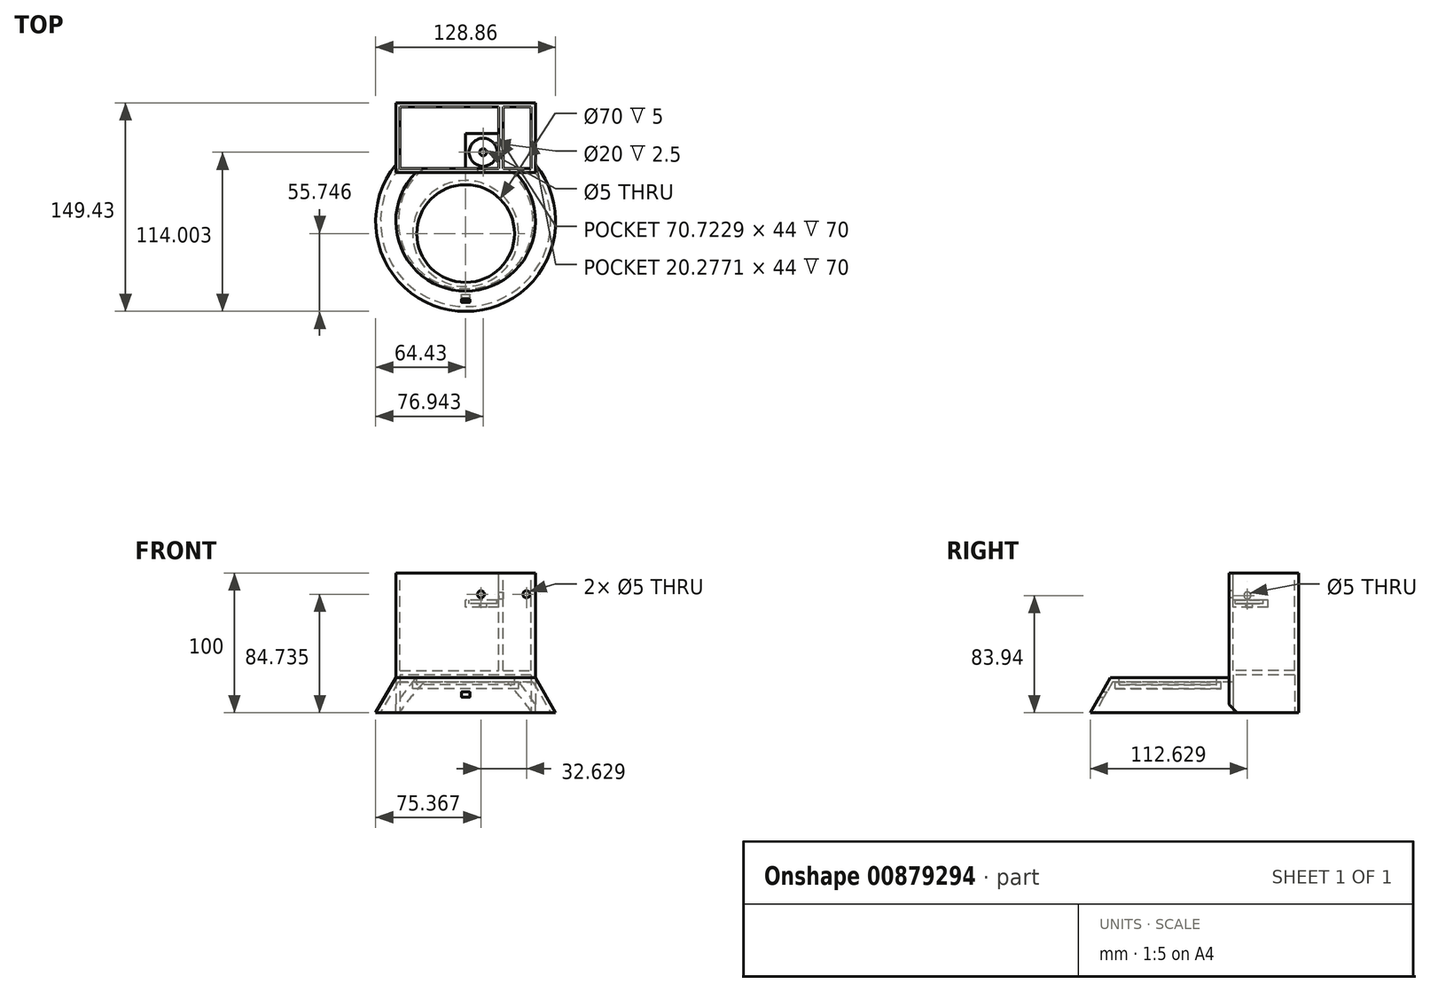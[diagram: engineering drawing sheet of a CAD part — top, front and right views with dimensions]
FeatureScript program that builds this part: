
annotation { "Feature Type Name" : "Feature", "Feature Type Description" : "" }
export const myFeature = defineFeature(function(context is Context, id is Id, definition is map)
    precondition{}
    {
        {
            var Q0;
            Q0=qCreatedBy(makeId("Top.planeOp"),FACE);
            var sketch = newSketch(context, id + "F0", { "sketchPlane" : qUnion([Q0])});
            skCircle(sketch, "E0", {"center": v(0, 0) * mm, "radius": 50 * mm});
            skSolve(sketch);
        }
        {
            var Q0;
            Q0 = qSketchRegion(id + "F0", true);
            extrude(context, id + "F1", {"entities" : qUnion([Q0]), "oppositeDirection" : true, "depth" : 25 * mm, "offsetDistance" : 25 * mm, "hasDraft" : true, "draftAngle" : 30 * degree});
        }
        {
            var Q0;
            Q0=makeQuery(id+"F1.opExtrude","CAP_FACE",FACE,{"disambiguationData":[OSD([sQuery(id+"F0.wireOp",EDGE,"E0")])],"isStart":false});
            var sketch = newSketch(context, id + "F2", { "sketchPlane" : qUnion([Q0])});
            skLineSegment(sketch, "E1.bottom", {"start": v(-50, -35) * mm, "end": v(50, -35) * mm});
            skLineSegment(sketch, "E1.top", {"start": v(-50, -85) * mm, "end": v(50, -85) * mm});
            skLineSegment(sketch, "E1.left", {"start": v(-50, -35) * mm, "end": v(-50, -85) * mm});
            skLineSegment(sketch, "E1.right", {"start": v(50, -35) * mm, "end": v(50, -85) * mm});
            skSolve(sketch);
        }
        {
            var Q0;
            {var subQ0=sQuery(id+"F2.wireOp",EDGE,"E1.bottom");Q0=makeQuery(id+"F2.imprint","IMPRINT",FACE,{"disambiguationData":[TD([[makeQuery(id+"F2.imprint","IMPRINT",EDGE,{"derivedFrom":subQ0}),-1.0]])]});}
            var Q1;
            {var subQ0=sQuery(id+"F2.wireOp",EDGE,"E1.top");Q1=makeQuery(id+"F2.imprint","IMPRINT",FACE,{"disambiguationData":[TD([[makeQuery(id+"F2.imprint","IMPRINT",EDGE,{"derivedFrom":subQ0}),1.0]])]});}
            extrude(context, id + "F3", {"entities" : qUnion([Q0, Q1]), "operationType" : NewBodyOperationType.ADD, "oppositeDirection" : true, "depth" : 100 * mm, "offsetDistance" : 25 * mm});
        }
        {
            var Q0;
            Q0=makeQuery(id+"F1.opExtrude","CAP_FACE",FACE,{"disambiguationData":[OSD([sQuery(id+"F0.wireOp",EDGE,"E0")])],"isStart":true});
            var sketch = newSketch(context, id + "F4", { "sketchPlane" : qUnion([Q0])});
            skCircle(sketch, "E2", {"center": v(0, -8.68) * mm, "radius": 35 * mm});
            skSolve(sketch);
        }
        {
            var Q0;
            Q0=makeQuery(id+"F4.imprint","IMPRINT",FACE,{"disambiguationData":[TD([[makeQuery(id+"F4.imprint","IMPRINT",EDGE,{"derivedFrom":sQuery(id+"F4.wireOp",EDGE,"E2")}),1.0]])]});
            extrude(context, id + "F5", {"entities" : qUnion([Q0]), "operationType" : NewBodyOperationType.REMOVE, "oppositeDirection" : true, "depth" : 5 * mm, "offsetDistance" : 25 * mm});
        }
        {
            var Q0;
            Q0=makeQuery(id+"F3.opExtrude","CAP_FACE",FACE,{"disambiguationData":[OSD([sQuery(id+"F2.wireOp",EDGE,"E1.bottom"),sQuery(id+"F2.wireOp",EDGE,"E1.top"),sQuery(id+"F2.wireOp",EDGE,"E1.left"),sQuery(id+"F2.wireOp",EDGE,"E1.right")])],"isStart":false});
            var sketch = newSketch(context, id + "F6", { "sketchPlane" : qUnion([Q0])});
            skLineSegment(sketch, "E3.bottom", {"start": v(-47, 82) * mm, "end": v(23.72, 82) * mm});
            skLineSegment(sketch, "E3.top", {"start": v(-47, 38) * mm, "end": v(23.72, 38) * mm});
            skLineSegment(sketch, "E3.left", {"start": v(-47, 82) * mm, "end": v(-47, 38) * mm});
            skLineSegment(sketch, "E3.right", {"start": v(23.72, 82) * mm, "end": v(23.72, 38) * mm});
            skSolve(sketch);
        }
        {
            var Q0;
            Q0=makeQuery(id+"F6.imprint","IMPRINT",FACE,{"disambiguationData":[TD([[makeQuery(id+"F6.imprint","IMPRINT",EDGE,{"derivedFrom":sQuery(id+"F6.wireOp",EDGE,"E3.bottom")}),-1.0]])]});
            extrude(context, id + "F7", {"entities" : qUnion([Q0]), "operationType" : NewBodyOperationType.REMOVE, "oppositeDirection" : true, "depth" : 70 * mm, "offsetDistance" : 25 * mm});
        }
        {
            var Q0;
            Q0=makeQuery(id+"F3.opExtrude","CAP_FACE",FACE,{"disambiguationData":[OSD([sQuery(id+"F2.wireOp",EDGE,"E1.bottom"),sQuery(id+"F2.wireOp",EDGE,"E1.top"),sQuery(id+"F2.wireOp",EDGE,"E1.left"),sQuery(id+"F2.wireOp",EDGE,"E1.right")])],"isStart":false});
            var sketch = newSketch(context, id + "F8", { "sketchPlane" : qUnion([Q0])});
            skLineSegment(sketch, "E4.bottom", {"start": v(26.72, 82) * mm, "end": v(47, 82) * mm});
            skLineSegment(sketch, "E4.top", {"start": v(26.72, 38) * mm, "end": v(47, 38) * mm});
            skLineSegment(sketch, "E4.left", {"start": v(26.72, 82) * mm, "end": v(26.72, 38) * mm});
            skLineSegment(sketch, "E4.right", {"start": v(47, 82) * mm, "end": v(47, 38) * mm});
            skSolve(sketch);
        }
        {
            var Q0;
            Q0=makeQuery(id+"F8.imprint","IMPRINT",FACE,{"disambiguationData":[TD([[makeQuery(id+"F8.imprint","IMPRINT",EDGE,{"derivedFrom":sQuery(id+"F8.wireOp",EDGE,"E4.bottom")}),-1.0]])]});
            extrude(context, id + "F9", {"entities" : qUnion([Q0]), "operationType" : NewBodyOperationType.REMOVE, "oppositeDirection" : true, "depth" : 70 * mm, "offsetDistance" : 25 * mm});
        }
        {
            var Q0;
            Q0=makeQuery(id+"F3.boolean.opBoolean","MERGE",FACE,{"derivedFrom":[makeQuery(id+"F1.opExtrude","CAP_FACE",FACE,{"disambiguationData":[OSD([sQuery(id+"F0.wireOp",EDGE,"E0")])],"isStart":false}),makeQuery(id+"F3.opExtrude","CAP_FACE",FACE,{"disambiguationData":[OSD([sQuery(id+"F2.wireOp",EDGE,"E1.bottom"),sQuery(id+"F2.wireOp",EDGE,"E1.top"),sQuery(id+"F2.wireOp",EDGE,"E1.left"),sQuery(id+"F2.wireOp",EDGE,"E1.right")])],"isStart":true})]});
            shell(context, id + "F10", {"entities" : qUnion([Q0]), "thickness" : 3 * mm});
        }
        {
            var Q0;
            Q0=makeQuery(id+"F9.boolean.opBoolean","COPY",FACE,{"derivedFrom":makeQuery(id+"F9.opExtrude","SWEPT_FACE",FACE,{"disambiguationData":[OSD([sQuery(id+"F8.wireOp",EDGE,"E4.left")])]})});
            var sketch = newSketch(context, id + "F11", { "sketchPlane" : qUnion([Q0])});
            skCircle(sketch, "E5", {"center": v(48.2, 58.94) * mm, "radius": 2.5 * mm});
            skSolve(sketch);
        }
        {
            var Q0;
            Q0=makeQuery(id+"F3.opExtrude","SWEPT_FACE",FACE,{"disambiguationData":[OSD([sQuery(id+"F2.wireOp",EDGE,"E1.bottom")])]});
            var sketch = newSketch(context, id + "F12", { "sketchPlane" : qUnion([Q0])});
            skCircle(sketch, "E6", {"center": v(10.94, 59.73) * mm, "radius": 2.5 * mm});
            skCircle(sketch, "E7", {"center": v(43.57, 59.73) * mm, "radius": 2.5 * mm});
            skSolve(sketch);
        }
        {
            var Q0;
            Q0=makeQuery(id+"F12.imprint","IMPRINT",FACE,{"disambiguationData":[TD([[makeQuery(id+"F12.imprint","IMPRINT",EDGE,{"derivedFrom":sQuery(id+"F12.wireOp",EDGE,"E6")}),1.0]])]});
            var Q1;
            Q1=makeQuery(id+"F12.imprint","IMPRINT",FACE,{"disambiguationData":[TD([[makeQuery(id+"F12.imprint","IMPRINT",EDGE,{"derivedFrom":sQuery(id+"F12.wireOp",EDGE,"E7")}),1.0]])]});
            extrude(context, id + "F13", {"entities" : qUnion([Q0, Q1]), "operationType" : NewBodyOperationType.REMOVE, "endBound" : BoundingType.UP_TO_NEXT, "oppositeDirection" : true, "depth" : 25 * mm, "offsetDistance" : 25 * mm});
        }
        {
            var Q0;
            Q0=makeQuery(id+"F11.imprint","IMPRINT",FACE,{"disambiguationData":[TD([[makeQuery(id+"F11.imprint","IMPRINT",EDGE,{"derivedFrom":sQuery(id+"F11.wireOp",EDGE,"E5")}),1.0]])]});
            extrude(context, id + "F14", {"entities" : qUnion([Q0]), "operationType" : NewBodyOperationType.REMOVE, "endBound" : BoundingType.UP_TO_NEXT, "oppositeDirection" : true, "depth" : 25 * mm, "offsetDistance" : 25 * mm});
        }
        {
            var Q0;
            Q0=makeQuery(id+"F7.boolean.opBoolean","COPY",FACE,{"derivedFrom":makeQuery(id+"F7.opExtrude","SWEPT_FACE",FACE,{"disambiguationData":[OSD([sQuery(id+"F6.wireOp",EDGE,"E3.top")])]})});
            var sketch = newSketch(context, id + "F15", { "sketchPlane" : qUnion([Q0])});
            skLineSegment(sketch, "E8.0", {"start": v(-23.72, 5) * mm, "end": v(-23.72, 75) * mm});
            skLineSegment(sketch, "E9.bottom", {"start": v(-23.72, 50.5) * mm, "end": v(0, 50.5) * mm});
            skLineSegment(sketch, "E9.top", {"start": v(-23.72, 55.5) * mm, "end": v(0, 55.5) * mm});
            skLineSegment(sketch, "E9.left", {"start": v(-23.72, 50.5) * mm, "end": v(-23.72, 55.5) * mm});
            skLineSegment(sketch, "E9.right", {"start": v(0, 50.5) * mm, "end": v(0, 55.5) * mm});
            skSolve(sketch);
        }
        {
            var Q0;
            Q0=makeQuery(id+"F15.imprint","IMPRINT",FACE,{"disambiguationData":[TD([[makeQuery(id+"F15.imprint","IMPRINT",EDGE,{"derivedFrom":sQuery(id+"F15.wireOp",EDGE,"E9.bottom")}),1.0]])]});
            extrude(context, id + "F16", {"entities" : qUnion([Q0]), "operationType" : NewBodyOperationType.ADD, "depth" : 25 * mm, "offsetDistance" : 25 * mm});
        }
        {
            var Q0;
            Q0=makeQuery(id+"F16.opExtrude","SWEPT_FACE",FACE,{"disambiguationData":[OSD([sQuery(id+"F15.wireOp",EDGE,"E9.top")])]});
            var sketch = newSketch(context, id + "F17", { "sketchPlane" : qUnion([Q0])});
            skCircle(sketch, "E10", {"center": v(12.51, 49.57) * mm, "radius": 10 * mm});
            skSolve(sketch);
        }
        {
            var Q0;
            Q0=makeQuery(id+"F17.imprint","IMPRINT",FACE,{"disambiguationData":[TD([[makeQuery(id+"F17.imprint","IMPRINT",EDGE,{"derivedFrom":sQuery(id+"F17.wireOp",EDGE,"E10")}),1.0]])]});
            extrude(context, id + "F18", {"entities" : qUnion([Q0]), "operationType" : NewBodyOperationType.REMOVE, "oppositeDirection" : true, "depth" : 2.5 * mm, "offsetDistance" : 25 * mm});
        }
        {
            var Q0;
            Q0=makeQuery(id+"F18.boolean.opBoolean","COPY",FACE,{"derivedFrom":makeQuery(id+"F18.opExtrude","CAP_FACE",FACE,{"disambiguationData":[OSD([sQuery(id+"F17.wireOp",EDGE,"E10")])],"isStart":false})});
            var sketch = newSketch(context, id + "F19", { "sketchPlane" : qUnion([Q0])});
            skCircle(sketch, "E11.0.0", {"center": v(12.51, 49.57) * mm, "radius": 10 * mm});
            skCircle(sketch, "E12", {"center": v(12.51, 49.57) * mm, "radius": 2.5 * mm});
            skSolve(sketch);
        }
        {
            var Q0;
            Q0=makeQuery(id+"F19.imprint","IMPRINT",FACE,{"disambiguationData":[TD([[makeQuery(id+"F19.imprint","IMPRINT",EDGE,{"derivedFrom":sQuery(id+"F19.wireOp",EDGE,"E12")}),1.0]])]});
            extrude(context, id + "F20", {"entities" : qUnion([Q0]), "operationType" : NewBodyOperationType.REMOVE, "endBound" : BoundingType.UP_TO_NEXT, "oppositeDirection" : true, "depth" : 25 * mm, "offsetDistance" : 25 * mm});
        }
        {
            var Q0;
            Q0=qCreatedBy(makeId("Front.planeOp"),FACE);
            var sketch = newSketch(context, id + "F21", { "sketchPlane" : qUnion([Q0])});
            skLineSegment(sketch, "E13.bottom", {"start": v(2.5, -10.03) * mm, "end": v(-2.5, -10.03) * mm});
            skLineSegment(sketch, "E13.top", {"start": v(2.5, -14.03) * mm, "end": v(-2.5, -14.03) * mm});
            skLineSegment(sketch, "E13.left", {"start": v(3, -10.53) * mm, "end": v(3, -13.53) * mm});
            skLineSegment(sketch, "E13.right", {"start": v(-3, -10.53) * mm, "end": v(-3, -13.53) * mm});
            skPoint(sketch, "E14.visualSharp", {"position": v(3, -10.03) * mm});
            skArc(sketch, "E14.filletArc", {"start": v(3, -10.53) * mm, "mid": v(2.85, -10.18) * mm, "end": v(2.5, -10.03) * mm});
            skPoint(sketch, "E15.visualSharp", {"position": v(3, -14.03) * mm});
            skArc(sketch, "E15.filletArc", {"start": v(2.5, -14.03) * mm, "mid": v(2.85, -13.88) * mm, "end": v(3, -13.53) * mm});
            skPoint(sketch, "E16.visualSharp", {"position": v(-3, -10.03) * mm});
            skArc(sketch, "E16.filletArc", {"start": v(-2.5, -10.03) * mm, "mid": v(-2.85, -10.18) * mm, "end": v(-3, -10.53) * mm});
            skPoint(sketch, "E17.visualSharp", {"position": v(-3, -14.03) * mm});
            skArc(sketch, "E17.filletArc", {"start": v(-3, -13.53) * mm, "mid": v(-2.85, -13.88) * mm, "end": v(-2.5, -14.03) * mm});
            skSolve(sketch);
        }
        {
            var Q0;
            Q0 = qSketchRegion(id + "F21", true);
            extrude(context, id + "F22", {"entities" : qUnion([Q0]), "operationType" : NewBodyOperationType.REMOVE, "depth" : 100 * mm, "offsetDistance" : 25 * mm});
        }
    });
